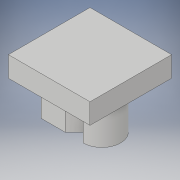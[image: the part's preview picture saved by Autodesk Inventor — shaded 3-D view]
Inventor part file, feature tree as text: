
AUTODESK INVENTOR PART (.ipt)
format: ipt  version: 2019 (Build 230136000, 136)  size: 119,296 bytes
history: native  units: mm
features: extrude x2, sketch x1
ambient origin geometry x8: Origin, YZ Plane, XZ Plane, XY Plane, X Axis, Y Axis, Z Axis, Center Point
bodies: Solid1 (feature_tree)
feature tree (3):
  sketch  "Sketch1"  dims[d0=20.0mm d1=20.0mm d2=2.5mm d3=2.5mm d4=2.5mm d8=2.5mm d9=9.0mm d10=2.5mm d11=2.5mm d12=10.0mm d13=0.0mm d14=5.0mm d15=0.0mm]
  extrude  "Extrusion1"  Depth=20.0mm
  extrude  "Extrusion2"  Depth=2.5mm
